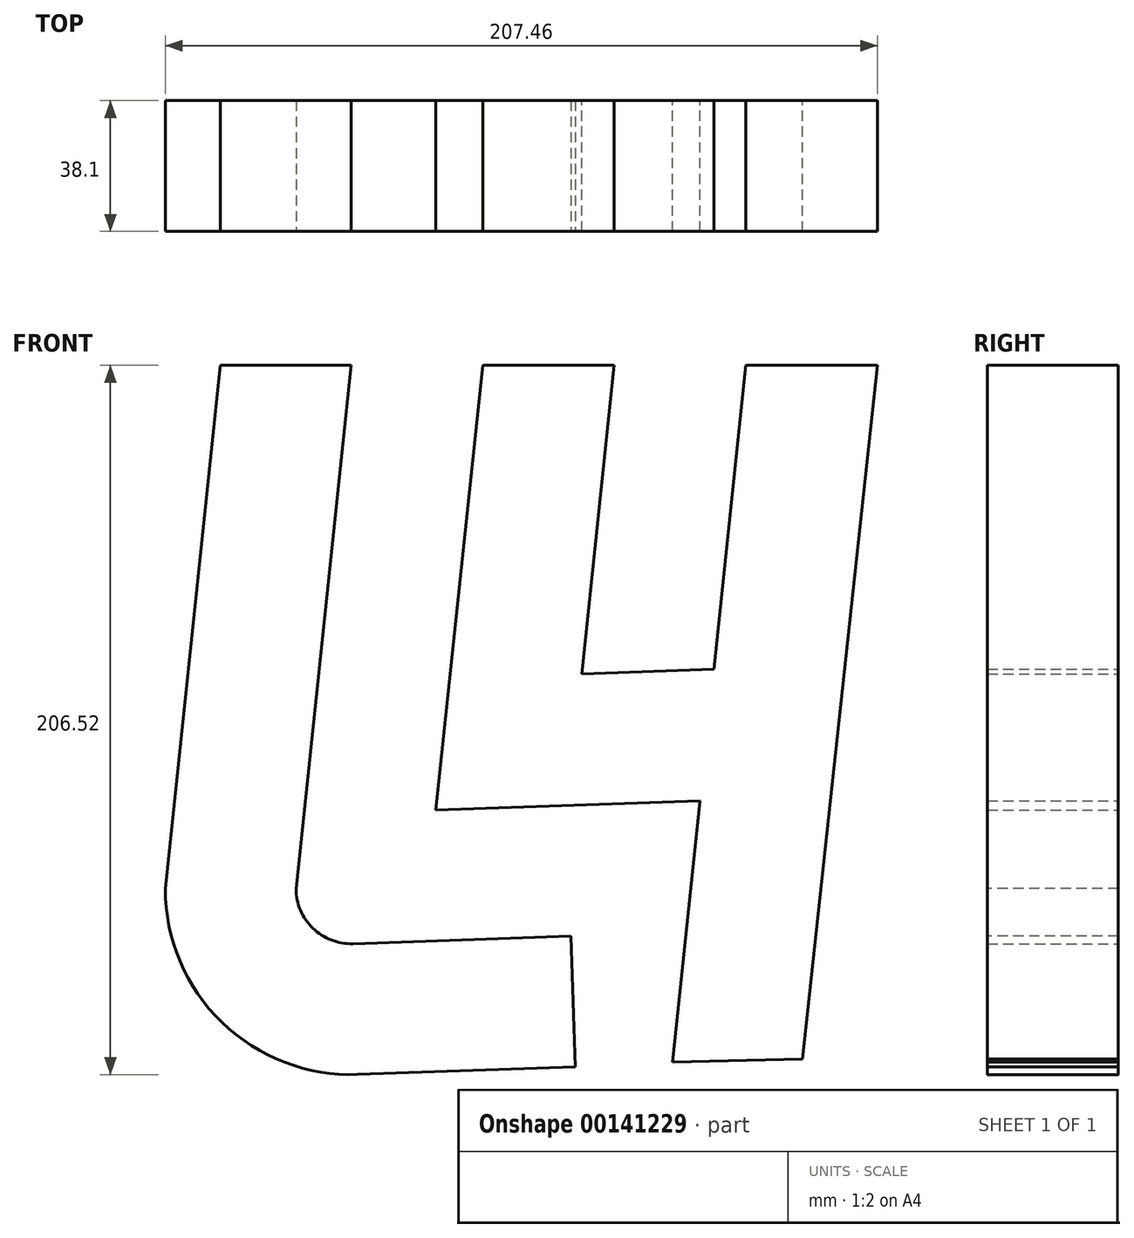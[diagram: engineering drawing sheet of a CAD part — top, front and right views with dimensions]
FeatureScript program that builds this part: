
annotation { "Feature Type Name" : "Feature", "Feature Type Description" : "" }
export const myFeature = defineFeature(function(context is Context, id is Id, definition is map)
    precondition{}
    {
        {
            var Q0;
            Q0=qCreatedBy(makeId("Top.planeOp"),FACE);
            cPlane(context, id + "F0", {"entities" : qUnion([Q0]), "cplaneType" : CPlaneType.OFFSET, "offset" : 76.2 * mm, "width" : 152.4 * mm, "height" : 152.4 * mm});
        }
        {
            var Q0;
            Q0=qCreatedBy(makeId("Front.planeOp"),FACE);
            var sketch = newSketch(context, id + "F1", { "sketchPlane" : qUnion([Q0])});
            skLineSegment(sketch, "E0", {"start": v(0, 0) * mm, "end": v(0, 76.2) * mm, "construction": true});
            skLineSegment(sketch, "E1", {"start": v(0, 0) * mm, "end": v(0, -76.2) * mm, "construction": true});
            skLineSegment(sketch, "E2", {"start": v(0, 76.2) * mm, "end": v(-16.02, -76.2) * mm});
            skSolve(sketch);
        }
        {
            var Q0;
            Q0=qCreatedBy(id+"F0.planeOp",FACE);
            var sketch = newSketch(context, id + "F2", { "sketchPlane" : qUnion([Q0])});
            skLineSegment(sketch, "E3.bottom", {"start": v(-19.05, 19.05) * mm, "end": v(19.05, 19.05) * mm});
            skLineSegment(sketch, "E3.top", {"start": v(-19.05, -19.05) * mm, "end": v(19.05, -19.05) * mm});
            skLineSegment(sketch, "E3.left", {"start": v(-19.05, 19.05) * mm, "end": v(-19.05, -19.05) * mm});
            skLineSegment(sketch, "E3.right", {"start": v(19.05, 19.05) * mm, "end": v(19.05, -19.05) * mm});
            skPoint(sketch, "E3.middle", {"position": v(0, 0) * mm});
            skSolve(sketch);
        }
        {
            var Q0;
            Q0=makeQuery(id+"F2.imprint","IMPRINT",FACE,{"disambiguationData":[TD([[makeQuery(id+"F2.imprint","IMPRINT",EDGE,{"derivedFrom":sQuery(id+"F2.wireOp",EDGE,"E3.bottom")}),-1.0]])]});
            var Q1;
            Q1=sQuery(id+"F1.wireOp",EDGE,"E2");
            sweep(context, id + "F3", {"profiles" : qUnion([Q0]), "path" : qUnion([Q1])});
        }
        {
            var Q0;
            Q0=qCreatedBy(makeId("Top.planeOp"),FACE);
            cPlane(context, id + "F4", {"entities" : qUnion([Q0]), "cplaneType" : CPlaneType.OFFSET, "offset" : 76.2 * mm, "oppositeDirection" : true, "width" : 152.4 * mm, "height" : 152.4 * mm});
        }
        {
            var Q0;
            Q0=qCreatedBy(id+"F4.planeOp",FACE);
            var sketch = newSketch(context, id + "F5", { "sketchPlane" : qUnion([Q0])});
            skLineSegment(sketch, "E4.0.0", {"start": v(3.03, -19.05) * mm, "end": v(3.03, 19.05) * mm});
            skLineSegment(sketch, "E4.0.1", {"start": v(3.03, 19.05) * mm, "end": v(19.05, 19.05) * mm});
            skLineSegment(sketch, "E4.0.2", {"start": v(19.05, 19.05) * mm, "end": v(19.05, -19.05) * mm});
            skLineSegment(sketch, "E4.0.3", {"start": v(19.05, -19.05) * mm, "end": v(3.03, -19.05) * mm});
            skSolve(sketch);
        }
        {
            var Q0;
            Q0=makeQuery(id+"F3.opSweep","CAP_FACE",FACE,{"disambiguationData":[OSD([sQuery(id+"F1.wireOp",VERTEX,"E2.end"),sQuery(id+"F2.wireOp",EDGE,"E3.bottom"),sQuery(id+"F2.wireOp",EDGE,"E3.top"),sQuery(id+"F2.wireOp",EDGE,"E3.left"),sQuery(id+"F2.wireOp",EDGE,"E3.right")])],"isStart":false});
            var Q1;
            Q1=sQuery(id+"F5.wireOp",EDGE,"E4.0.2");
            revolve(context, id + "F6", {"operationType" : NewBodyOperationType.ADD, "entities" : qUnion([Q0]), "axis" : qUnion([Q1]), "revolveType" : RevolveType.ONE_DIRECTION, "angle" : 92 * degree});
        }
        {
            var Q0;
            Q0=makeQuery(id+"F6.opRevolve","CAP_FACE",FACE,{"disambiguationData":[OSD([sQuery(id+"F1.wireOp",VERTEX,"E2.end"),sQuery(id+"F2.wireOp",EDGE,"E3.bottom"),sQuery(id+"F2.wireOp",EDGE,"E3.top"),sQuery(id+"F2.wireOp",EDGE,"E3.left"),sQuery(id+"F2.wireOp",EDGE,"E3.right")])],"isStart":false});
            extrude(context, id + "F7", {"entities" : qUnion([Q0]), "operationType" : NewBodyOperationType.ADD, "depth" : 63.5 * mm});
        }
        {
            var Q0;
            Q0=qCreatedBy(makeId("Front.planeOp"),FACE);
            cPlane(context, id + "F8", {"entities" : qUnion([Q0]), "cplaneType" : CPlaneType.OFFSET, "offset" : 19.05 * mm, "oppositeDirection" : true, "width" : 152.4 * mm, "height" : 152.4 * mm});
        }
        {
            var Q0;
            Q0=qCreatedBy(id+"F8.planeOp",FACE);
            var sketch = newSketch(context, id + "F9", { "sketchPlane" : qUnion([Q0])});
            skLineSegment(sketch, "E5.0.0", {"start": v(-19.05, 76.2) * mm, "end": v(-35.07, -76.2) * mm});
            skArc(sketch, "E5.0.1", {"start": v(-35.07, -76.2) * mm, "mid": v(-18.54, -115.13) * mm, "end": v(20.94, -130.28) * mm});
            skLineSegment(sketch, "E5.0.2", {"start": v(20.94, -130.28) * mm, "end": v(84.4, -128.07) * mm});
            skLineSegment(sketch, "E5.0.3", {"start": v(83.07, -90) * mm, "end": v(84.4, -128.07) * mm});
            skLineSegment(sketch, "E5.0.4", {"start": v(83.07, -90) * mm, "end": v(19.6, -92.2) * mm});
            skArc(sketch, "E5.0.5", {"start": v(19.6, -92.2) * mm, "mid": v(7.92, -87.72) * mm, "end": v(3.03, -76.2) * mm});
            skLineSegment(sketch, "E5.0.6", {"start": v(3.03, -76.2) * mm, "end": v(19.05, 76.2) * mm});
            skLineSegment(sketch, "E5.0.7", {"start": v(19.05, 76.2) * mm, "end": v(-19.05, 76.2) * mm});
            skLineSegment(sketch, "E6", {"start": v(10.4, -6.16) * mm, "end": v(48.28, -10.14) * mm, "construction": true});
            skLineSegment(sketch, "E7", {"start": v(72.94, -90.35) * mm, "end": v(71.61, -52.27) * mm, "construction": true});
            skLineSegment(sketch, "E8", {"start": v(48.28, -10.14) * mm, "end": v(57.36, 76.2) * mm});
            skLineSegment(sketch, "E9", {"start": v(48.28, -10.14) * mm, "end": v(43.75, -53.24) * mm});
            skLineSegment(sketch, "E10", {"start": v(57.36, 76.2) * mm, "end": v(95.67, 76.2) * mm});
            skLineSegment(sketch, "E11", {"start": v(95.67, 76.2) * mm, "end": v(86.23, -13.64) * mm});
            skLineSegment(sketch, "E12", {"start": v(53.57, 40.16) * mm, "end": v(91.46, 36.18) * mm, "construction": true});
            skLineSegment(sketch, "E13", {"start": v(86.23, -13.64) * mm, "end": v(124.68, -12.3) * mm});
            skLineSegment(sketch, "E14", {"start": v(43.75, -53.24) * mm, "end": v(120.66, -50.56) * mm});
            skLineSegment(sketch, "E15", {"start": v(105.45, -12.96) * mm, "end": v(106.78, -51.04) * mm, "construction": true});
            skLineSegment(sketch, "E16", {"start": v(124.68, -12.3) * mm, "end": v(133.98, 76.2) * mm});
            skLineSegment(sketch, "E17", {"start": v(89.94, 21.65) * mm, "end": v(127.83, 17.67) * mm, "construction": true});
            skLineSegment(sketch, "E18", {"start": v(120.66, -50.56) * mm, "end": v(112.65, -126.7) * mm});
            skLineSegment(sketch, "E19", {"start": v(133.98, 76.2) * mm, "end": v(172.39, 76.2) * mm});
            skLineSegment(sketch, "E20", {"start": v(172.39, 76.2) * mm, "end": v(150.53, -125.76) * mm});
            skLineSegment(sketch, "E21", {"start": v(112.65, -126.7) * mm, "end": v(150.53, -125.76) * mm});
            skLineSegment(sketch, "E22", {"start": v(131.07, 48.5) * mm, "end": v(168.96, 44.52) * mm, "construction": true});
            skSolve(sketch);
        }
        {
            var Q0;
            Q0=makeQuery(id+"F9.imprint","IMPRINT",FACE,{"disambiguationData":[TD([[makeQuery(id+"F9.imprint","IMPRINT",EDGE,{"derivedFrom":sQuery(id+"F9.wireOp",EDGE,"E8")}),-1.0]])]});
            extrude(context, id + "F10", {"entities" : qUnion([Q0]), "depth" : 38.1 * mm});
        }
    });
